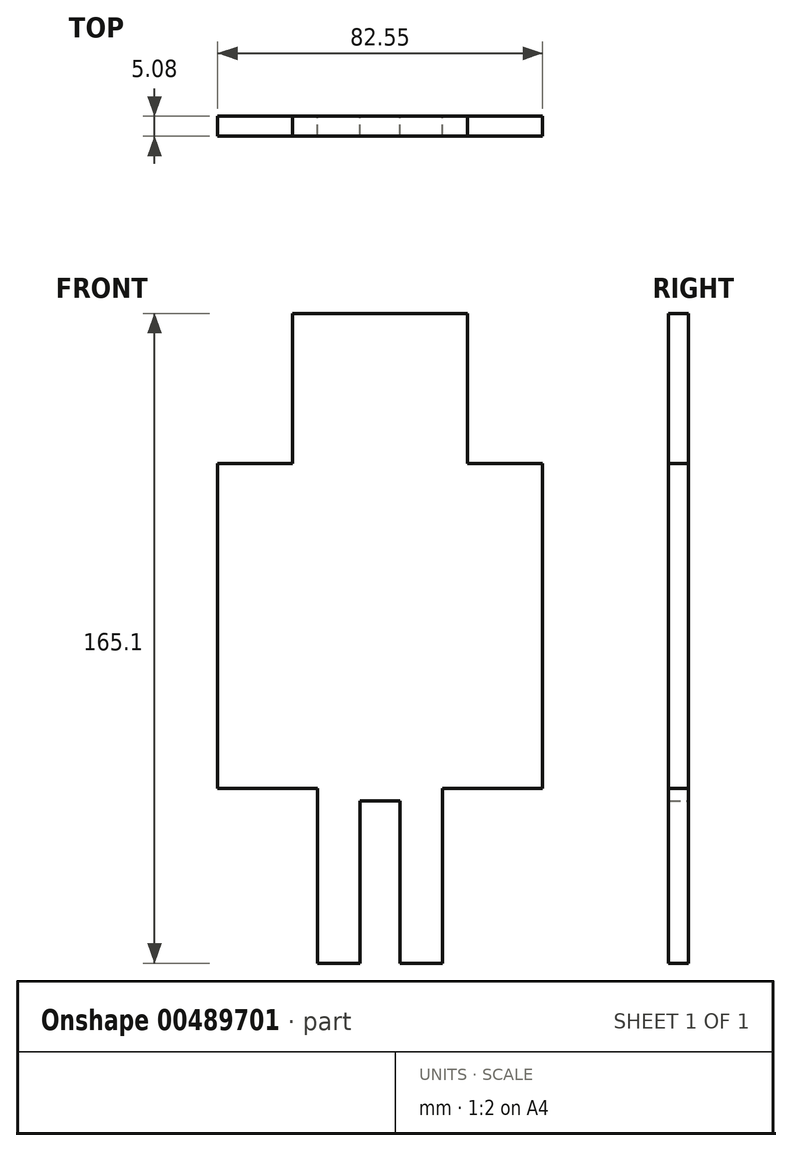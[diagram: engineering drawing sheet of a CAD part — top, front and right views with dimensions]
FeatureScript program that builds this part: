
annotation { "Feature Type Name" : "Feature", "Feature Type Description" : "" }
export const myFeature = defineFeature(function(context is Context, id is Id, definition is map)
    precondition{}
    {
        {
            var Q0;
            Q0=qCreatedBy(makeId("Front.planeOp"),FACE);
            var sketch = newSketch(context, id + "F0", { "sketchPlane" : qUnion([Q0])});
            skLineSegment(sketch, "E0.bottom", {"start": v(-98.33, 141.97) * mm, "end": v(-53.88, 141.97) * mm});
            skLineSegment(sketch, "E0.top", {"start": v(-91.98, -23.13) * mm, "end": v(-81.18, -23.13) * mm});
            skLineSegment(sketch, "E0.left", {"start": v(-117.38, 103.87) * mm, "end": v(-117.38, 21.32) * mm});
            skLineSegment(sketch, "E0.right", {"start": v(-34.83, 103.87) * mm, "end": v(-34.83, 21.32) * mm});
            skLineSegment(sketch, "E1.top", {"start": v(-117.38, 103.87) * mm, "end": v(-98.33, 103.87) * mm});
            skLineSegment(sketch, "E1.right", {"start": v(-98.33, 141.97) * mm, "end": v(-98.33, 103.87) * mm});
            skLineSegment(sketch, "E2.top", {"start": v(-34.83, 103.87) * mm, "end": v(-53.88, 103.87) * mm});
            skLineSegment(sketch, "E2.right", {"start": v(-53.88, 141.97) * mm, "end": v(-53.88, 103.87) * mm});
            skLineSegment(sketch, "E3.top", {"start": v(-117.38, 21.32) * mm, "end": v(-91.98, 21.32) * mm});
            skLineSegment(sketch, "E3.right", {"start": v(-91.98, -23.13) * mm, "end": v(-91.98, 21.32) * mm});
            skLineSegment(sketch, "E4.top", {"start": v(-34.83, 21.32) * mm, "end": v(-60.23, 21.32) * mm});
            skLineSegment(sketch, "E4.right", {"start": v(-60.23, -23.13) * mm, "end": v(-60.23, 21.32) * mm});
            skLineSegment(sketch, "E5.bottom", {"start": v(-81.18, 18.14) * mm, "end": v(-71.02, 18.14) * mm});
            skLineSegment(sketch, "E5.left", {"start": v(-81.18, 18.14) * mm, "end": v(-81.18, -23.13) * mm});
            skLineSegment(sketch, "E5.right", {"start": v(-71.02, 18.14) * mm, "end": v(-71.02, -23.13) * mm});
            skPoint(sketch, "E5.middle", {"position": v(-76.1, -23.13) * mm});
            skPoint(sketch, "E5.top.end.orphan", {"position": v(-71.02, -64.4) * mm});
            skPoint(sketch, "E5.top.start.orphan", {"position": v(-81.18, -64.4) * mm});
            skLineSegment(sketch, "E6.trimOffspring", {"start": v(-71.02, -23.13) * mm, "end": v(-60.23, -23.13) * mm});
            skSolve(sketch);
        }
        {
            var Q0;
            Q0=makeQuery(id+"F0.imprint","IMPRINT",FACE,{"disambiguationData":[TD([[makeQuery(id+"F0.imprint","IMPRINT",EDGE,{"derivedFrom":sQuery(id+"F0.wireOp",EDGE,"E0.bottom")}),-1.0]])]});
            extrude(context, id + "F1", {"entities" : qUnion([Q0]), "depth" : 5.08 * mm});
        }
    });
